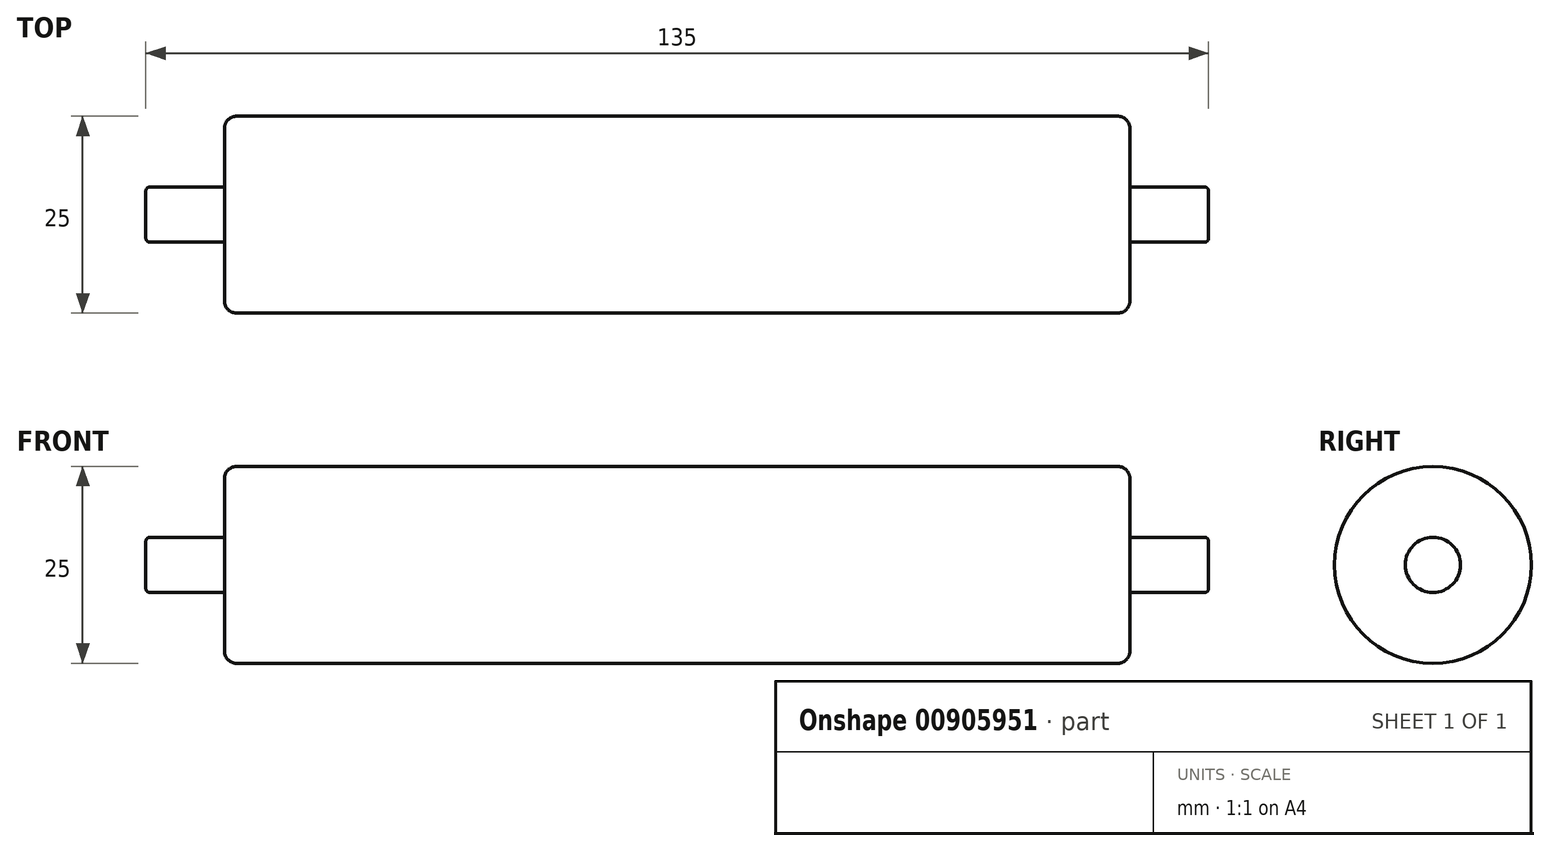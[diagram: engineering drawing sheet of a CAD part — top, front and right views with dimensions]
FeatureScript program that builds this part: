
annotation { "Feature Type Name" : "Feature", "Feature Type Description" : "" }
export const myFeature = defineFeature(function(context is Context, id is Id, definition is map)
    precondition{}
    {
        {
            var Q0;
            Q0=qCreatedBy(makeId("Right.planeOp"),FACE);
            var sketch = newSketch(context, id + "F0", { "sketchPlane" : qUnion([Q0])});
            skCircle(sketch, "E0", {"center": v(0, 0) * mm, "radius": 12.5 * mm});
            skSolve(sketch);
        }
        {
            var Q0;
            Q0 = qSketchRegion(id + "F0", true);
            extrude(context, id + "F1", {"entities" : qUnion([Q0]), "endBound" : BoundingType.SYMMETRIC, "depth" : 115 * mm, "offsetDistance" : 25 * mm});
        }
        {
            var Q0;
            Q0=makeQuery(id+"F1.opExtrude","CAP_FACE",FACE,{"disambiguationData":[OSD([sQuery(id+"F0.wireOp",EDGE,"E0")])],"isStart":true});
            var sketch = newSketch(context, id + "F2", { "sketchPlane" : qUnion([Q0])});
            skCircle(sketch, "E1", {"center": v(0, 0) * mm, "radius": 3.5 * mm});
            skSolve(sketch);
        }
        {
            var Q0;
            Q0 = qSketchRegion(id + "F2", true);
            extrude(context, id + "F3", {"entities" : qUnion([Q0]), "operationType" : NewBodyOperationType.ADD, "depth" : 10 * mm, "offsetDistance" : 25 * mm});
        }
        {
            var Q0;
            Q0=makeQuery(id+"F1.opExtrude","SWEPT_BODY",BODY,{"disambiguationData":[OSD([sQuery(id+"F0.wireOp",EDGE,"E0")])]});
            var Q1;
            Q1=qCreatedBy(makeId("Right.planeOp"),FACE);
            mirror(context, id + "F4", {"operationType" : NewBodyOperationType.ADD, "entities" : qUnion([Q0]), "mirrorPlane" : qUnion([Q1])});
        }
        {
            var Q0;
            Q0=makeQuery(id+"F1.opExtrude","CAP_EDGE",EDGE,{"disambiguationData":[OSD([sQuery(id+"F0.wireOp",EDGE,"E0")])],"isStart":true});
            var Q1;
            Q1=makeQuery(id+"F1.opExtrude","CAP_EDGE",EDGE,{"disambiguationData":[OSD([sQuery(id+"F0.wireOp",EDGE,"E0")])],"isStart":false});
            fillet(context, id + "F5", {"entities" : qUnion([Q0, Q1]), "radius" : 1.5 * mm, "tangentPropagation" : true, "allowEdgeOverflow" : false});
        }
        {
            var Q0;
            Q0=makeQuery(id+"F4.opPattern","COPY",EDGE,{"derivedFrom":makeQuery(id+"F3.opExtrude","CAP_EDGE",EDGE,{"disambiguationData":[OSD([sQuery(id+"F2.wireOp",EDGE,"E1")])],"isStart":false}),"instanceName":"1"});
            var Q1;
            Q1=makeQuery(id+"F3.opExtrude","CAP_EDGE",EDGE,{"disambiguationData":[OSD([sQuery(id+"F2.wireOp",EDGE,"E1")])],"isStart":false});
            fillet(context, id + "F6", {"entities" : qUnion([Q0, Q1]), "radius" : .5 * mm, "tangentPropagation" : true, "allowEdgeOverflow" : false});
        }
    });
